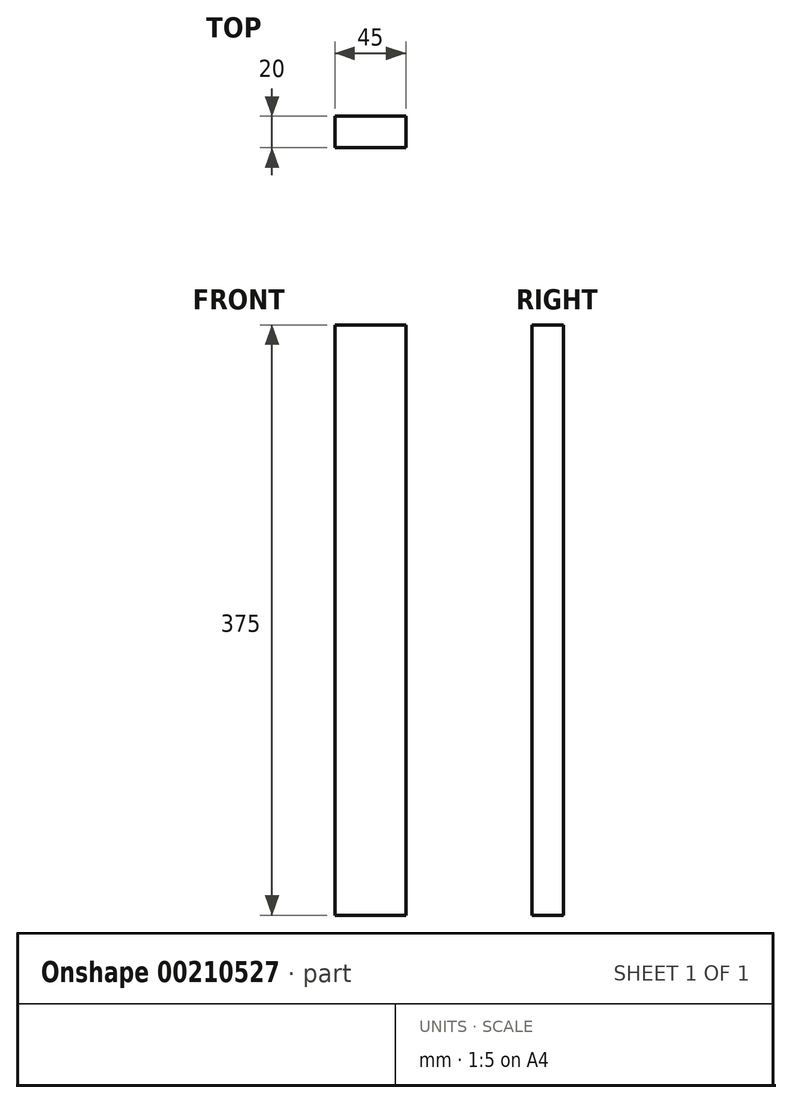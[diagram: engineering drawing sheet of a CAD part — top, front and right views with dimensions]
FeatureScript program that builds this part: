
annotation { "Feature Type Name" : "Feature", "Feature Type Description" : "" }
export const myFeature = defineFeature(function(context is Context, id is Id, definition is map)
    precondition{}
    {
        {
            var Q0;
            Q0=qCreatedBy(makeId("Top.planeOp"),FACE);
            var sketch = newSketch(context, id + "F0", { "sketchPlane" : qUnion([Q0])});
            skLineSegment(sketch, "E0.bottom", {"start": v(-20.6, 7.04) * mm, "end": v(24.4, 7.04) * mm});
            skLineSegment(sketch, "E0.top", {"start": v(-20.6, -12.96) * mm, "end": v(24.4, -12.96) * mm});
            skLineSegment(sketch, "E0.left", {"start": v(-20.6, 7.04) * mm, "end": v(-20.6, -12.96) * mm});
            skLineSegment(sketch, "E0.right", {"start": v(24.4, 7.04) * mm, "end": v(24.4, -12.96) * mm});
            skSolve(sketch);
        }
        {
            var Q0;
            Q0=makeQuery(id+"F0.imprint","IMPRINT",FACE,{"disambiguationData":[TD([[makeQuery(id+"F0.imprint","IMPRINT",EDGE,{"derivedFrom":sQuery(id+"F0.wireOp",EDGE,"E0.bottom")}),-1.0]])]});
            extrude(context, id + "F1", {"entities" : qUnion([Q0]), "depth" : 375 * mm});
        }
    });
